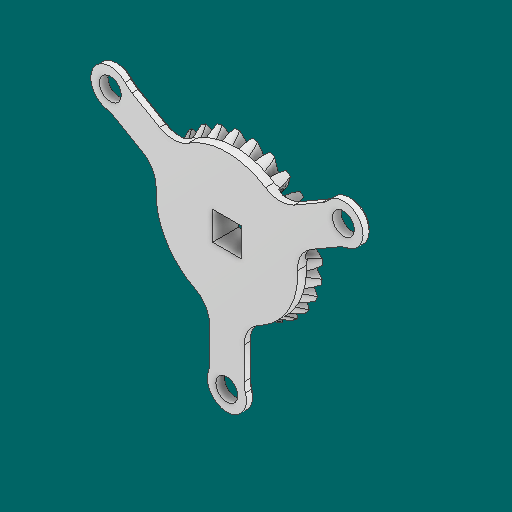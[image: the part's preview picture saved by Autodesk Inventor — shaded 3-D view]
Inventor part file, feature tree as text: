
AUTODESK INVENTOR PART (.ipt)
format: ipt  version: 2023.1 (Build 271208000, 208)  size: 758,272 bytes
history: native  units: in
note: dims shown in document units (in); Inventor stores cm internally (conversion verified against a paired STEP export)
features: other x30, sketch x3
ambient origin geometry x8: Origin, YZ Plane, XZ Plane, XY Plane, X Axis, Y Axis, Z Axis, Center Point
bodies: Solid1 (feature_tree)
feature tree (33):
  other  "Bevel Gear2"
  other  "Solid1::Bevel Gear2"
  other  "TaggingFeature1"
  other  "Teeth Body Sketch"
  other  "Start Sketch"
  other  "End Sketch"
  other  "End Sketch Right"
  other  "End Sketch Left"
  other  "Body Sketch"
  sketch  "Sketch6"  dims[d0=0.3937in]
  sketch  "Sketch8"  dims[d48=0.0in]
  sketch  "Sketch9"  dims[d49=0.0in d50=90.0deg d52=0.0in d53=0.0in d54=0.0in]
  other  "3D Sketch Right"
  other  "3D Sketch Left"
  other  "Mesh Plane"
  other  "Top Plane"
  other  "Mesh Plane2"
  other  "Tooth Plane"
  other  "End Plane"
  other  "End Plane Right"
  other  "End Plane Left"
  other  "Z Axis_1"
  other  "Top Point"
  other  "Start Point"
  other  "End Point"
  other  "Srf1"
  other  "Srf1::Derived"
  other  "Start plane iMate"
  other  "Mesh iMate2"
  other  "Axis Angle iMate"
  other  "Axis iMate"
  other  "Mesh iMate"
  other  "Intersection iMate"
